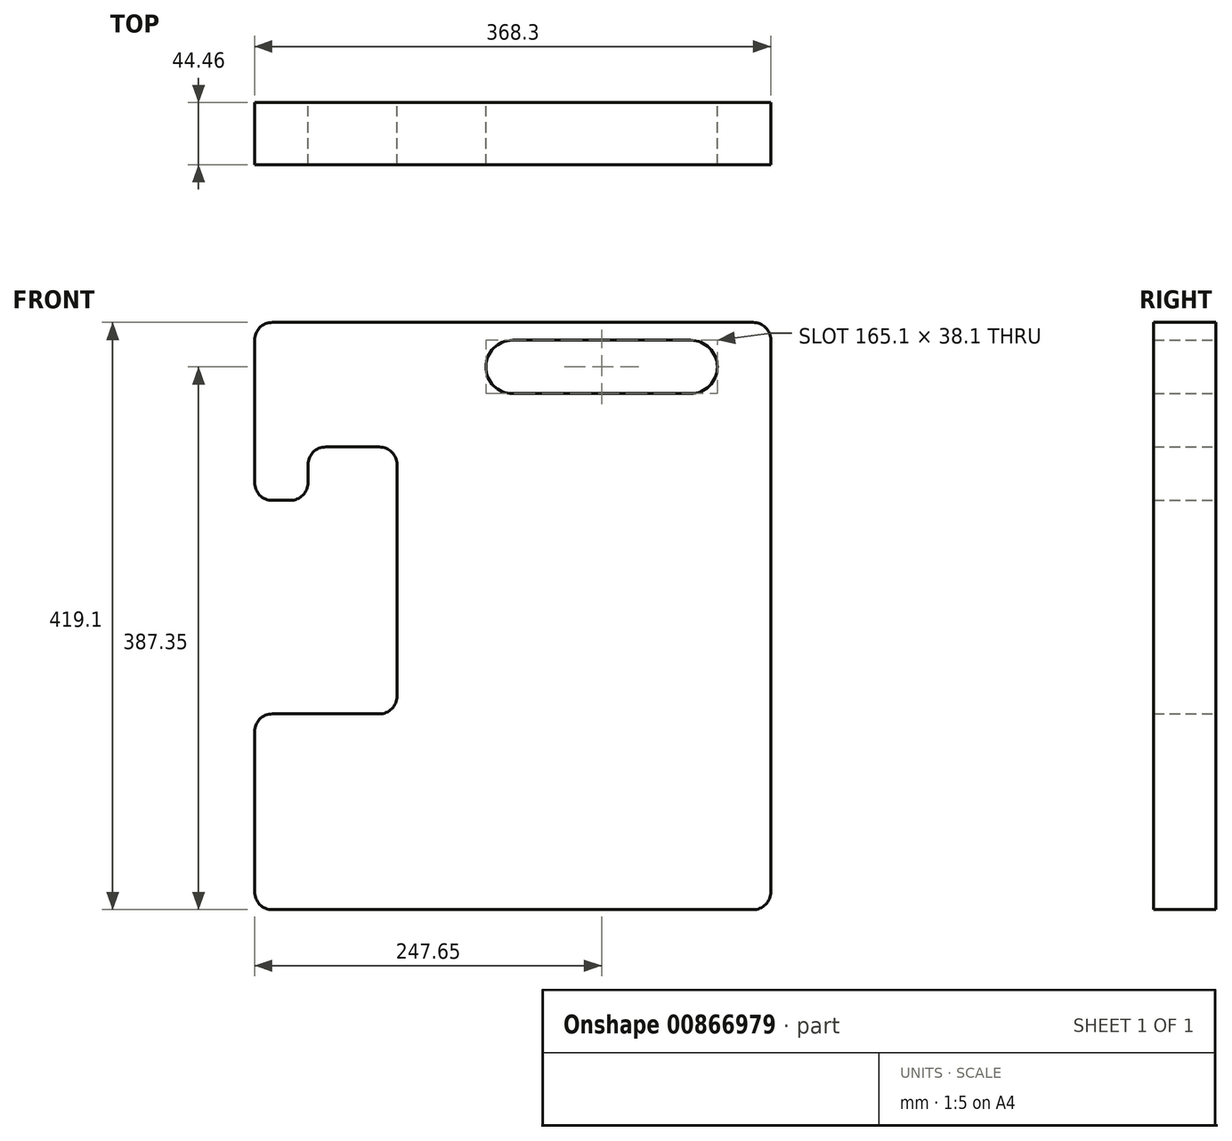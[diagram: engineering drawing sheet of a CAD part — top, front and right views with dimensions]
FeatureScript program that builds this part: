
annotation { "Feature Type Name" : "Feature", "Feature Type Description" : "" }
export const myFeature = defineFeature(function(context is Context, id is Id, definition is map)
    precondition{}
    {
        {
            var Q0;
            Q0=qCreatedBy(makeId("Front.planeOp"),FACE);
            var sketch = newSketch(context, id + "F0", { "sketchPlane" : qUnion([Q0]), "disableImprinting" : false});
            skLineSegment(sketch, "E0.bottom", {"start": v(184.15, -209.55) * mm, "end": v(-184.15, -209.55) * mm});
            skLineSegment(sketch, "E0.top", {"start": v(184.15, 209.55) * mm, "end": v(-184.15, 209.55) * mm});
            skLineSegment(sketch, "E0.left", {"start": v(184.15, -209.55) * mm, "end": v(184.15, 209.55) * mm});
            skPoint(sketch, "E0.middle", {"position": v(0, 0) * mm});
            skArc(sketch, "E1", {"start": v(0, 196.85) * mm, "mid": v(-19.05, 177.8) * mm, "end": v(0, 158.75) * mm});
            skArc(sketch, "E2", {"start": v(127, 158.75) * mm, "mid": v(146.05, 177.8) * mm, "end": v(127, 196.85) * mm});
            skLineSegment(sketch, "E3", {"start": v(0, 196.85) * mm, "end": v(127, 196.85) * mm});
            skLineSegment(sketch, "E4", {"start": v(0, 158.75) * mm, "end": v(127, 158.75) * mm});
            skLineSegment(sketch, "E5", {"start": v(-184.15, -69.85) * mm, "end": v(-82.55, -69.85) * mm});
            skLineSegment(sketch, "E6", {"start": v(-82.55, -69.85) * mm, "end": v(-82.55, 120.65) * mm});
            skLineSegment(sketch, "E7", {"start": v(-82.55, 120.65) * mm, "end": v(-146.05, 120.65) * mm});
            skLineSegment(sketch, "E8", {"start": v(-184.15, -69.85) * mm, "end": v(-184.15, -209.55) * mm});
            skLineSegment(sketch, "E9", {"start": v(-146.05, 120.65) * mm, "end": v(-146.05, 82.55) * mm});
            skLineSegment(sketch, "E10", {"start": v(-146.05, 82.55) * mm, "end": v(-184.15, 82.55) * mm});
            skLineSegment(sketch, "E11", {"start": v(-184.15, 209.55) * mm, "end": v(-184.15, 82.55) * mm});
            skSolve(sketch);
        }
        {
            var Q0;
            Q0=makeQuery(id+"F0.imprint","IMPRINT",FACE,{"disambiguationData":[TD([[makeQuery(id+"F0.imprint","IMPRINT",EDGE,{"derivedFrom":sQuery(id+"F0.wireOp",EDGE,"E0.bottom")}),-1.0]])]});
            extrude(context, id + "F1", {"entities" : qUnion([Q0]), "flatOperationType" : FlatOperationType.REMOVE, "depth" : 44.45 * mm, "offsetDistance" : 25.4 * mm, "domain" : OperationDomain.MODEL, "symmetric" : true});
        }
        {
            var Q0;
            Q0=makeQuery(id+"F1.opExtrude","SWEPT_EDGE",EDGE,{"disambiguationData":[OSD([sQuery(id+"F0.wireOp",EDGE,"E0.top"),sQuery(id+"F0.wireOp",EDGE,"E11")])]});
            var Q1;
            Q1=makeQuery(id+"F1.opExtrude","SWEPT_EDGE",EDGE,{"disambiguationData":[OSD([sQuery(id+"F0.wireOp",EDGE,"E0.top"),sQuery(id+"F0.wireOp",EDGE,"E0.left")])]});
            var Q2;
            Q2=makeQuery(id+"F1.opExtrude","SWEPT_EDGE",EDGE,{"disambiguationData":[OSD([sQuery(id+"F0.wireOp",EDGE,"E0.bottom"),sQuery(id+"F0.wireOp",EDGE,"E0.left")])]});
            var Q3;
            Q3=makeQuery(id+"F1.opExtrude","SWEPT_EDGE",EDGE,{"disambiguationData":[OSD([sQuery(id+"F0.wireOp",EDGE,"E0.bottom"),sQuery(id+"F0.wireOp",EDGE,"E8")])]});
            fillet(context, id + "F2", {"entities" : qUnion([Q0, Q1, Q2, Q3]), "radius" : 12.7 * mm, "tangentPropagation" : true, "allowEdgeOverflow" : false});
        }
        {
            var Q0;
            Q0=makeQuery(id+"F1.opExtrude","SWEPT_EDGE",EDGE,{"disambiguationData":[OSD([sQuery(id+"F0.wireOp",EDGE,"E10"),sQuery(id+"F0.wireOp",EDGE,"E11")])]});
            var Q1;
            Q1=makeQuery(id+"F1.opExtrude","SWEPT_EDGE",EDGE,{"disambiguationData":[OSD([sQuery(id+"F0.wireOp",EDGE,"E9"),sQuery(id+"F0.wireOp",EDGE,"E10")])]});
            var Q2;
            Q2=makeQuery(id+"F1.opExtrude","SWEPT_EDGE",EDGE,{"disambiguationData":[OSD([sQuery(id+"F0.wireOp",EDGE,"E7"),sQuery(id+"F0.wireOp",EDGE,"E9")])]});
            var Q3;
            Q3=makeQuery(id+"F1.opExtrude","SWEPT_EDGE",EDGE,{"disambiguationData":[OSD([sQuery(id+"F0.wireOp",EDGE,"E6"),sQuery(id+"F0.wireOp",EDGE,"E7")])]});
            var Q4;
            Q4=makeQuery(id+"F1.opExtrude","SWEPT_EDGE",EDGE,{"disambiguationData":[OSD([sQuery(id+"F0.wireOp",EDGE,"E5"),sQuery(id+"F0.wireOp",EDGE,"E6")])]});
            var Q5;
            Q5=makeQuery(id+"F1.opExtrude","SWEPT_EDGE",EDGE,{"disambiguationData":[OSD([sQuery(id+"F0.wireOp",EDGE,"E5"),sQuery(id+"F0.wireOp",EDGE,"E8")])]});
            fillet(context, id + "F3", {"entities" : qUnion([Q0, Q1, Q2, Q3, Q4, Q5]), "radius" : 12.7 * mm, "tangentPropagation" : true, "allowEdgeOverflow" : false});
        }
    });
